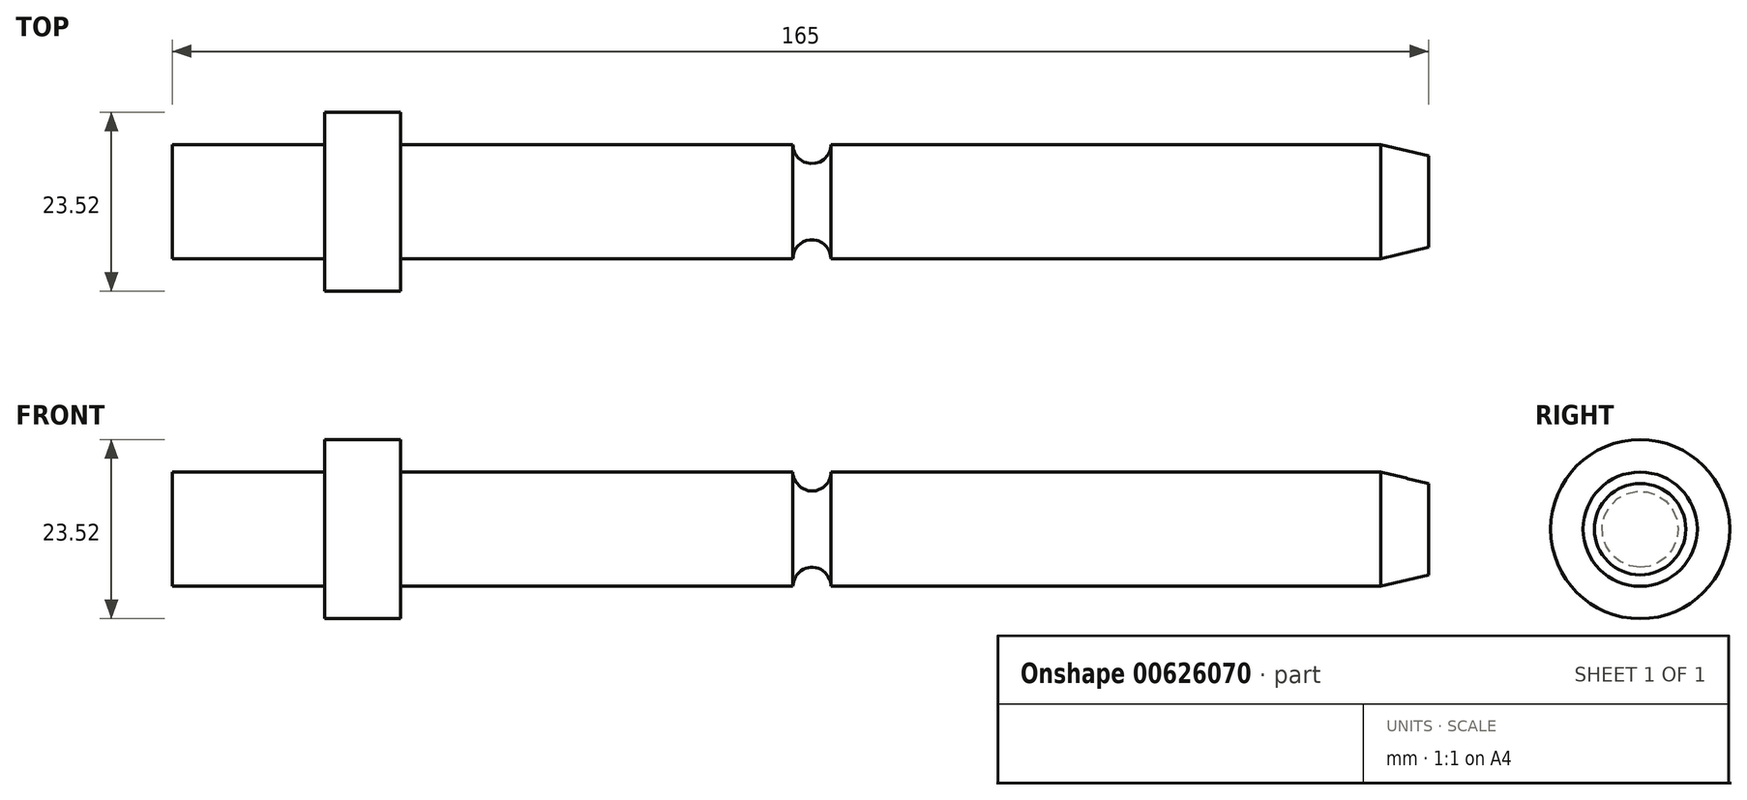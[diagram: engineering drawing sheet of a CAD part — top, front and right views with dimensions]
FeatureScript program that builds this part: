
annotation { "Feature Type Name" : "Feature", "Feature Type Description" : "" }
export const myFeature = defineFeature(function(context is Context, id is Id, definition is map)
    precondition{}
    {
        {
            var Q0;
            Q0=qCreatedBy(makeId("Front.planeOp"),FACE);
            var sketch = newSketch(context, id + "F0", { "sketchPlane" : qUnion([Q0])});
            skLineSegment(sketch, "E0.bottom", {"start": v(0, 0) * mm, "end": v(165, 0) * mm});
            skLineSegment(sketch, "E0.top", {"start": v(0, 7.5) * mm, "end": v(158.68, 7.5) * mm});
            skLineSegment(sketch, "E0.left", {"start": v(0, 0) * mm, "end": v(0, 7.5) * mm});
            skLineSegment(sketch, "E0.right", {"start": v(165, 0) * mm, "end": v(165, 6) * mm});
            skLineSegment(sketch, "E1", {"start": v(165, 6) * mm, "end": v(158.68, 7.5) * mm});
            skSolve(sketch);
        }
        {
            var Q0;
            Q0=makeQuery(id+"F0.imprint","IMPRINT",FACE,{"disambiguationData":[TD([[makeQuery(id+"F0.imprint","IMPRINT",EDGE,{"derivedFrom":sQuery(id+"F0.wireOp",EDGE,"E0.bottom")}),1.0]])]});
            var Q1;
            Q1=sQuery(id+"F0.wireOp",EDGE,"E0.bottom");
            revolve(context, id + "F1", {"entities" : qUnion([Q0]), "axis" : qUnion([Q1]), "revolveType" : RevolveType.FULL});
        }
        {
            var Q0;
            Q0=qCreatedBy(makeId("Right.planeOp"),FACE);
            cPlane(context, id + "F2", {"entities" : qUnion([Q0]), "cplaneType" : CPlaneType.OFFSET, "offset" : 20 * mm, "width" : 150 * mm, "height" : 150 * mm});
        }
        {
            var Q0;
            Q0=qCreatedBy(id+"F2.planeOp",FACE);
            var sketch = newSketch(context, id + "F3", { "sketchPlane" : qUnion([Q0])});
            skCircle(sketch, "E2", {"center": v(0, 0) * mm, "radius": 11.76 * mm});
            skSolve(sketch);
        }
        {
            var Q0;
            Q0=makeQuery(id+"F3.imprint","IMPRINT",FACE,{"disambiguationData":[TD([[makeQuery(id+"F3.imprint","IMPRINT",EDGE,{"derivedFrom":sQuery(id+"F3.wireOp",EDGE,"E2")}),1.0]])]});
            extrude(context, id + "F4", {"entities" : qUnion([Q0]), "operationType" : NewBodyOperationType.ADD, "depth" : 10 * mm, "offsetDistance" : 25 * mm});
        }
        {
            var Q0;
            Q0=qCreatedBy(makeId("Front.planeOp"),FACE);
            var sketch = newSketch(context, id + "F5", { "sketchPlane" : qUnion([Q0])});
            skCircle(sketch, "E3", {"center": v(84, 7.5) * mm, "radius": 2.5 * mm});
            skSolve(sketch);
        }
        {
            var Q0;
            Q0=qCreatedBy(makeId("Front.planeOp"),FACE);
            var sketch = newSketch(context, id + "F6", { "sketchPlane" : qUnion([Q0])});
            skLineSegment(sketch, "E4", {"start": v(-12.86, 0) * mm, "end": v(199.41, 0) * mm, "construction": true});
            skSolve(sketch);
        }
        {
            var Q0;
            Q0=makeQuery(id+"F5.imprint","IMPRINT",FACE,{"disambiguationData":[TD([[makeQuery(id+"F5.imprint","IMPRINT",EDGE,{"derivedFrom":sQuery(id+"F5.wireOp",EDGE,"E3")}),1.0]])]});
            var Q1;
            Q1=sQuery(id+"F6.wireOp",EDGE,"E4");
            revolve(context, id + "F7", {"operationType" : NewBodyOperationType.REMOVE, "entities" : qUnion([Q0]), "axis" : qUnion([Q1]), "revolveType" : RevolveType.FULL, "oppositeDirection" : true});
        }
    });
